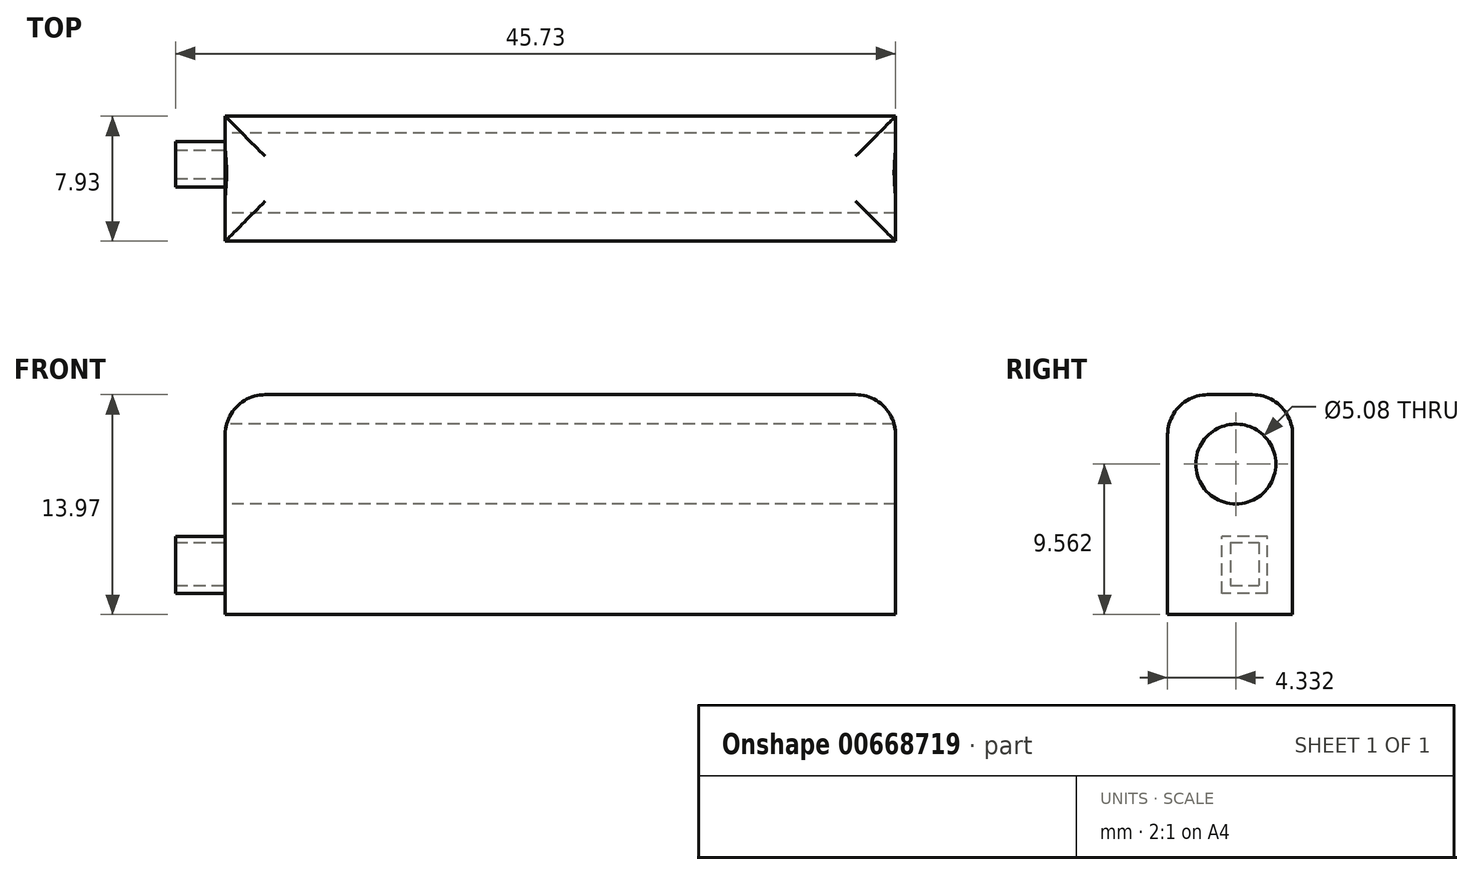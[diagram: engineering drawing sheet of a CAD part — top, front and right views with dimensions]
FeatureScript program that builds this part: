
annotation { "Feature Type Name" : "Feature", "Feature Type Description" : "" }
export const myFeature = defineFeature(function(context is Context, id is Id, definition is map)
    precondition{}
    {
        {
            var Q0;
            Q0=qCreatedBy(makeId("Top.planeOp"),FACE);
            var sketch = newSketch(context, id + "F0", { "sketchPlane" : qUnion([Q0])});
            skLineSegment(sketch, "E0.bottom", {"start": v(0, 0) * mm, "end": v(42.58, 0) * mm});
            skLineSegment(sketch, "E0.top", {"start": v(0, 7.93) * mm, "end": v(42.58, 7.93) * mm});
            skLineSegment(sketch, "E0.left", {"start": v(0, 0) * mm, "end": v(0, 7.93) * mm});
            skLineSegment(sketch, "E0.right", {"start": v(42.58, 0) * mm, "end": v(42.58, 7.93) * mm});
            skSolve(sketch);
        }
        {
            var Q0;
            Q0=makeQuery(id+"F0.imprint","IMPRINT",FACE,{"disambiguationData":[TD([[makeQuery(id+"F0.imprint","IMPRINT",EDGE,{"derivedFrom":sQuery(id+"F0.wireOp",EDGE,"E0.bottom")}),1.0]])]});
            extrude(context, id + "F1", {"entities" : qUnion([Q0]), "depth" : 13.97 * mm, "offsetDistance" : 25.4 * mm});
        }
        {
            var Q0;
            Q0=qCreatedBy(makeId("Right.planeOp"),FACE);
            var sketch = newSketch(context, id + "F2", { "sketchPlane" : qUnion([Q0])});
            skCircle(sketch, "E1", {"center": v(4.33, 9.56) * mm, "radius": 2.54 * mm});
            skSolve(sketch);
        }
        {
            var Q0;
            Q0=makeQuery(id+"F2.imprint","IMPRINT",FACE,{"disambiguationData":[TD([[makeQuery(id+"F2.imprint","IMPRINT",EDGE,{"derivedFrom":sQuery(id+"F2.wireOp",EDGE,"E1")}),1.0]])]});
            extrude(context, id + "F3", {"entities" : qUnion([Q0]), "operationType" : NewBodyOperationType.REMOVE, "depth" : 45.03 * mm, "offsetDistance" : 25.4 * mm});
        }
        {
            var Q0;
            Q0=makeQuery(id+"F1.opExtrude","CAP_EDGE",EDGE,{"disambiguationData":[OSD([sQuery(id+"F0.wireOp",EDGE,"E0.left")])],"isStart":false});
            var Q1;
            Q1=makeQuery(id+"F1.opExtrude","CAP_EDGE",EDGE,{"disambiguationData":[OSD([sQuery(id+"F0.wireOp",EDGE,"E0.top")])],"isStart":false});
            var Q2;
            Q2=makeQuery(id+"F1.opExtrude","CAP_EDGE",EDGE,{"disambiguationData":[OSD([sQuery(id+"F0.wireOp",EDGE,"E0.bottom")])],"isStart":false});
            var Q3;
            Q3=makeQuery(id+"F1.opExtrude","CAP_EDGE",EDGE,{"disambiguationData":[OSD([sQuery(id+"F0.wireOp",EDGE,"E0.right")])],"isStart":false});
            fillet(context, id + "F4", {"entities" : qUnion([Q0, Q1, Q2, Q3]), "radius" : 2.54 * mm, "tangentPropagation" : true, "allowEdgeOverflow" : false});
        }
        {
            var Q0;
            Q0=qCreatedBy(makeId("Right.planeOp"),FACE);
            var sketch = newSketch(context, id + "F5", { "sketchPlane" : qUnion([Q0])});
            skLineSegment(sketch, "E2.bottom", {"start": v(6.33, 1.35) * mm, "end": v(3.45, 1.35) * mm});
            skLineSegment(sketch, "E2.top", {"start": v(6.33, 4.95) * mm, "end": v(3.45, 4.95) * mm});
            skLineSegment(sketch, "E2.left", {"start": v(6.33, 1.35) * mm, "end": v(6.33, 4.95) * mm});
            skLineSegment(sketch, "E2.right", {"start": v(3.45, 1.35) * mm, "end": v(3.45, 4.95) * mm});
            skLineSegment(sketch, "E3.bottom", {"start": v(4, 4.59) * mm, "end": v(5.79, 4.59) * mm});
            skLineSegment(sketch, "E3.top", {"start": v(4, 1.85) * mm, "end": v(5.79, 1.85) * mm});
            skLineSegment(sketch, "E3.left", {"start": v(4, 4.59) * mm, "end": v(4, 1.85) * mm});
            skLineSegment(sketch, "E3.right", {"start": v(5.79, 4.59) * mm, "end": v(5.79, 1.85) * mm});
            skSolve(sketch);
        }
        {
            var Q0;
            Q0=makeQuery(id+"F5.imprint","IMPRINT",FACE,{"disambiguationData":[TD([[makeQuery(id+"F5.imprint","IMPRINT",EDGE,{"derivedFrom":sQuery(id+"F5.wireOp",EDGE,"E2.bottom")}),-1.0]])]});
            extrude(context, id + "F6", {"entities" : qUnion([Q0]), "operationType" : NewBodyOperationType.ADD, "oppositeDirection" : true, "depth" : 3.15 * mm, "offsetDistance" : 25.4 * mm});
        }
    });
